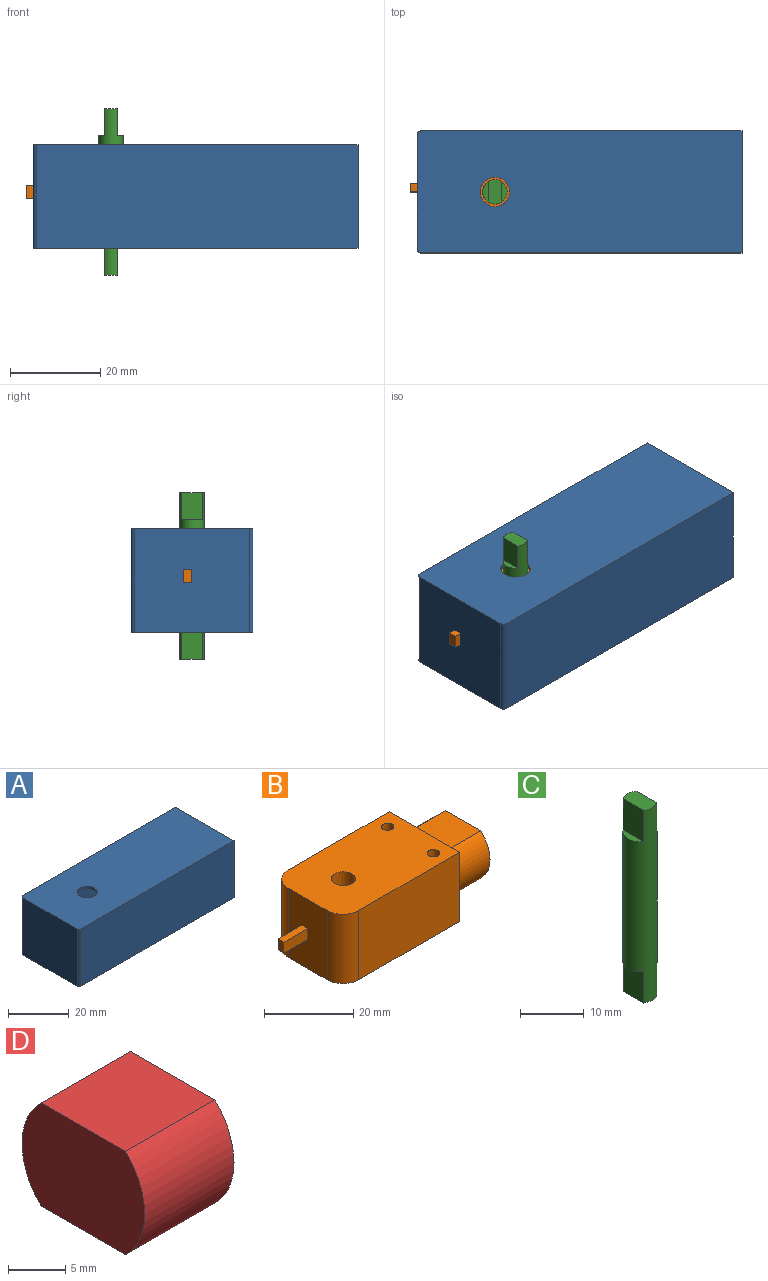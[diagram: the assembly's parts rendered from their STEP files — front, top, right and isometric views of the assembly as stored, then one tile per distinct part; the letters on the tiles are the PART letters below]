
ASSEMBLY  parts=4 mates=3
PART A: 13 faces, bbox 72x27x23 mm
  f0: plane 27x23mm, normal (1,0,0), area 71mm2, adj f2,f3,f4,f5,f7,f8,f10
  f1: plane 25.4x23mm, normal (-1,0,0), area 584.2mm2, adj f2,f10,f11,f12
  f2: plane 72x27mm, normal (0,0,1), area 1910.5mm2, adj f0,f1,f3,f4,f9,f11,f12
  f3: plane 71.2x23mm, normal (0,-1,0), area 1637.6mm2, adj f0,f2,f10,f12
  f4: plane 71.2x23mm, normal (0,1,0), area 1637.6mm2, adj f0,f2,f10,f11
  f5: plane 71x25mm, normal (0,0,-1), area 1741.8mm2, adj f0,f6,f7,f8,f9
  f6: plane 25x22mm, normal (1,0,0), area 550mm2, adj f5,f7,f8,f10
  f7: plane 71x22mm, normal (0,1,0), area 1562mm2, adj f0,f5,f6,f10
  f8: plane 71x22mm, normal (0,-1,0), area 1562mm2, adj f0,f5,f6,f10
  f9: cylinder r=3.25mm len=6.5mm, axis (0,0,1), area 20.4mm2, adj f2,f5
  f10: plane 72x27mm, normal (0,0,-1), area 168.7mm2, adj f0,f1,f3,f4,f6,f7,f8,f11
  f11: cylinder r=0.8mm len=23mm, axis (0,0,-1), area 28.9mm2, adj f1,f2,f4,f10
  f12: cylinder r=0.8mm len=23mm, axis (0,0,1), area 28.9mm2, adj f1,f2,f3,f10
PART B: 36 faces, bbox 56.8x22.3x19 mm
  f0: plane 17.1x13mm, normal (1,0,0), area 48.5mm2, adj f17,f18,f19,f20,f32,f33,f34,f35
  f1: plane 22.3x19mm, normal (1,0,0), area 225.2mm2, adj f2,f9,f10,f11,f17,f18,f19,f20
  f2: plane 32x19mm, normal (0,1,0), area 608mm2, adj f1,f3,f10,f11
  f3: cylinder r=5mm len=19mm, axis (0,0,-1), area 149.2mm2, adj f2,f4,f10,f11
  f4: plane 19x12.3mm, normal (-1,0,0), area 228.1mm2, adj f3,f5,f10,f11,f12,f14,f15,f16
  f5: cylinder r=5mm len=19mm, axis (0,0,-1), area 149.2mm2, adj f4,f9,f10,f11
  f6: cylinder r=1.4mm len=19mm, axis (0,0,-1), area 167.1mm2, adj f10,f11
  f7: cylinder r=1.4mm len=19mm, axis (0,0,-1), area 167.1mm2, adj f10,f11
  f8: cylinder r=2.7mm len=19mm, axis (0,0,-1), area 322.3mm2, adj f10,f11
  f9: plane 32x19mm, normal (0,-1,0), area 608mm2, adj f1,f5,f10,f11
  f10: plane 37x22.3mm, normal (0,0,1), area 779.2mm2, adj f1,f2,f3,f4,f5,f6,f7,f8
  f11: plane 37x22.3mm, normal (0,0,-1), area 779.2mm2, adj f1,f2,f3,f4,f5,f6,f7,f8
  f12: plane 7.53x3mm, normal (0,1,0), area 22.6mm2, adj f4,f13,f15,f16
  f13: plane 3x1.88mm, normal (-1,0,0), area 5.6mm2, adj f12,f14,f15,f16
  f14: plane 7.53x3mm, normal (0,-1,0), area 22.6mm2, adj f4,f13,f15,f16
  f15: plane 7.53x1.88mm, normal (0,0,1), area 14.2mm2, adj f4,f12,f13,f14
  f16: plane 7.53x1.88mm, normal (0,0,-1), area 14.2mm2, adj f4,f12,f13,f14
  f17: plane 12.25x11.11mm, normal (0,0,-1), area 136.1mm2, adj f0,f1,f18,f20
  f18: cylinder r=8.55mm len=13mm, axis (-1,0,0), area 180.9mm2, adj f0,f1,f17,f19
  f19: plane 12.25x11.11mm, normal (0,0,1), area 136.1mm2, adj f0,f1,f18,f20
  f20: cylinder r=8.55mm len=13mm, axis (-1,0,0), area 180.9mm2, adj f0,f1,f17,f19
  f21: plane 20.3x17mm, normal (-1,0,0), area 195.2mm2, adj f22,f29,f30,f31,f32,f33,f34,f35
  f22: plane 31x17mm, normal (0,-1,0), area 527mm2, adj f21,f23,f30,f31
  f23: cylinder r=4mm len=17mm, axis (0,0,-1), area 106.8mm2, adj f22,f24,f30,f31
  f24: plane 17x12.3mm, normal (1,0,0), area 209.1mm2, adj f23,f25,f30,f31
  f25: cylinder r=4mm len=17mm, axis (0,0,-1), area 106.8mm2, adj f24,f29,f30,f31
  f26: cylinder r=2.4mm len=17mm, axis (0,0,-1), area 256.4mm2, adj f30,f31
  f27: cylinder r=2.4mm len=17mm, axis (0,0,-1), area 256.4mm2, adj f30,f31
  f28: cylinder r=3.7mm len=17mm, axis (0,0,-1), area 395.2mm2, adj f30,f31
  f29: plane 31x17mm, normal (0,1,0), area 527mm2, adj f21,f25,f30,f31
  f30: plane 35x20.3mm, normal (0,0,-1), area 624.4mm2, adj f21,f22,f23,f24,f25,f26,f27,f28
  f31: plane 35x20.3mm, normal (0,0,1), area 624.4mm2, adj f21,f22,f23,f24,f25,f26,f27,f28
  f32: plane 13.25x10.34mm, normal (0,0,1), area 137.1mm2, adj f0,f21,f33,f35
  f33: cylinder r=7.55mm len=13.25mm, axis (-1,0,0), area 163.3mm2, adj f0,f21,f32,f34
  f34: plane 13.25x10.34mm, normal (0,0,-1), area 137.1mm2, adj f0,f21,f33,f35
  f35: cylinder r=7.55mm len=13.25mm, axis (-1,0,0), area 163.3mm2, adj f0,f21,f32,f34
PART C: 11 faces, bbox 5.4x5.4x37 mm
  f0: plane 5.4x3.05mm, normal (0,0,-1), area 15.6mm2, adj f2,f7,f9
  f1: plane 5.4x2.98mm, normal (0,0,1), area 15.2mm2, adj f2,f3,f5
  f2: cylinder r=2.7mm len=37mm, axis (0,0,-1), area 500.9mm2, adj f0,f1,f3,f4,f5,f6,f7,f8
  f3: plane 6x4.5mm, normal (1,0,0), area 27mm2, adj f1,f2,f4
  f4: plane 4.5x1.21mm, normal (0,0,1), area 3.8mm2, adj f2,f3
  f5: plane 6x4.5mm, normal (-1,0,0), area 27mm2, adj f1,f2,f6
  f6: plane 4.5x1.21mm, normal (0,0,1), area 3.8mm2, adj f2,f5
  f7: plane 6x4.45mm, normal (1,0,0), area 26.7mm2, adj f0,f2,f8
  f8: plane 4.45x1.17mm, normal (0,0,-1), area 3.7mm2, adj f2,f7
  f9: plane 6x4.45mm, normal (-1,0,0), area 26.7mm2, adj f0,f2,f10
  f10: plane 4.45x1.17mm, normal (0,0,-1), area 3.7mm2, adj f2,f9
PART D: 6 faces, bbox 11x15.1x11 mm
  f0: plane 11x10.34mm, normal (0,0,-1), area 113.8mm2, adj f1,f3,f4,f5
  f1: cylinder r=7.55mm len=11mm, axis (-1,0,0), area 135.6mm2, adj f0,f2,f4,f5
  f2: plane 11x10.34mm, normal (0,0,1), area 113.8mm2, adj f1,f3,f4,f5
  f3: cylinder r=7.55mm len=11mm, axis (-1,0,0), area 135.6mm2, adj f0,f2,f4,f5
  f4: plane 15.1x11mm, normal (1,0,0), area 149.9mm2, adj f0,f1,f2,f3
  f5: plane 15.1x11mm, normal (-1,0,0), area 149.9mm2, adj f0,f1,f2,f3
PLACE A t=(12.57,-25.88,17.57)mm
PLACE B t=(1.02,-39.38,19.07)mm
PLACE C t=(1.02,-39.38,19.07)mm
PLACE D rot(axis=(0,1,0),180deg) t=(73.52,-39.38,19.07)mm
MATE fastened D.f1 <-> B.f18  axis (-1,0,0) through (31.77,-39.38,19.07)mm
MATE fastened A.f9 <-> B.f8  axis (0,0,-1) through (-6.18,-39.38,28.57)mm
MATE fastened C.f2 <-> B.f8  axis (0,0,-1) through (-6.18,-39.38,19.07)mm
